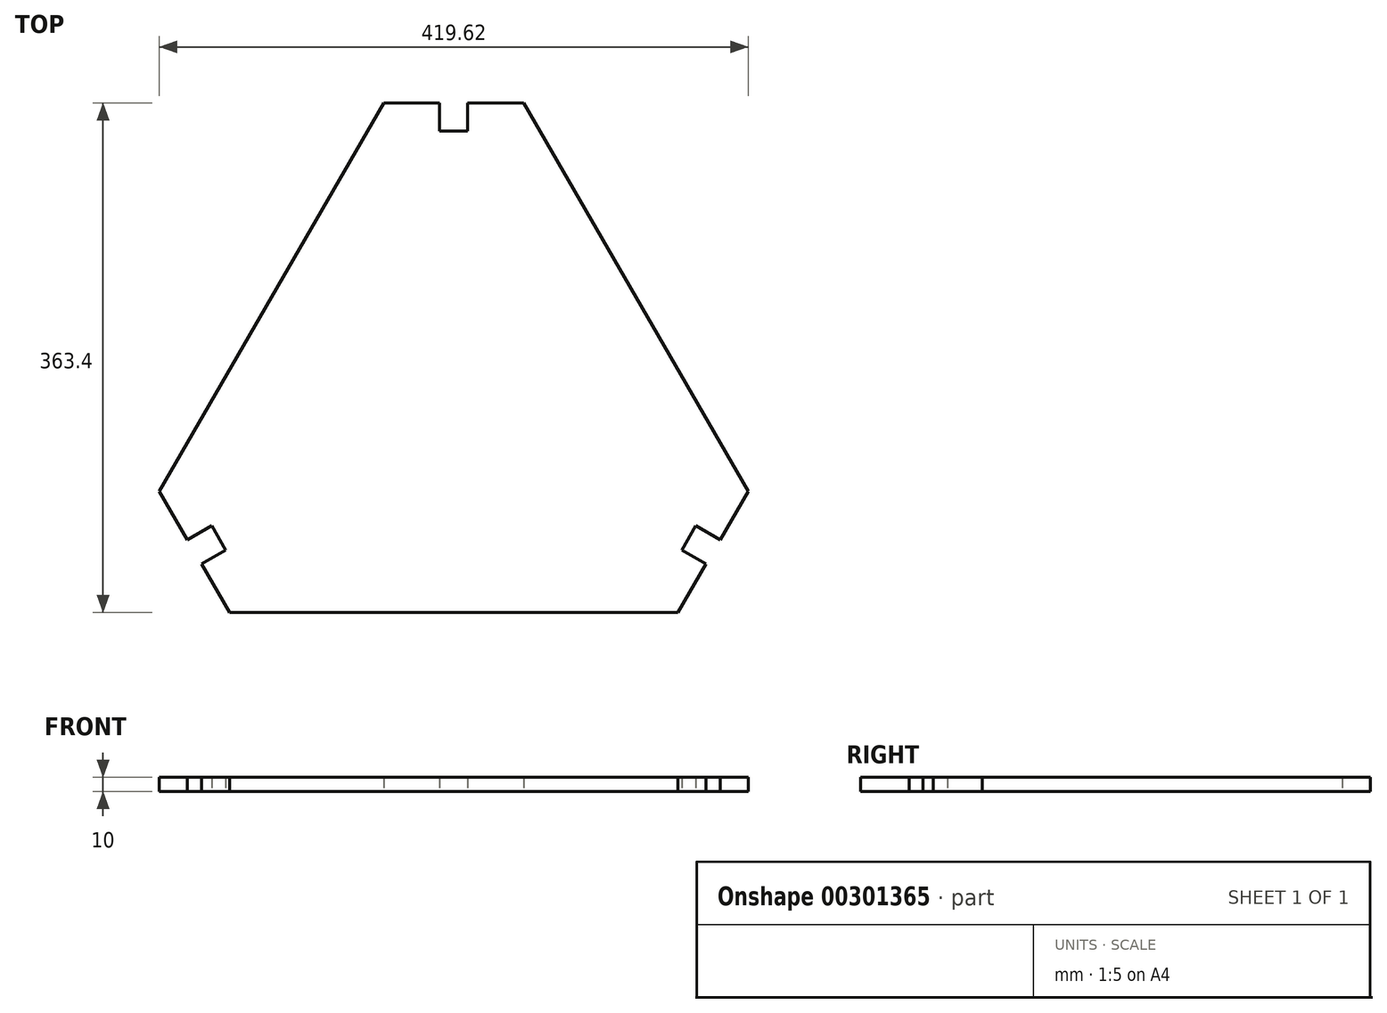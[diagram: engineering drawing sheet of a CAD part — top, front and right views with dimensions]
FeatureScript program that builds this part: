
annotation { "Feature Type Name" : "Feature", "Feature Type Description" : "" }
export const myFeature = defineFeature(function(context is Context, id is Id, definition is map)
    precondition{}
    {
        {
            var Q0;
            Q0=qCreatedBy(makeId("Top.planeOp"),FACE);
            var sketch = newSketch(context, id + "F0", { "sketchPlane" : qUnion([Q0])});
            skCircle(sketch, "E0.cCircle", {"center": v(0, 0) * mm, "radius": 213.4 * mm, "construction": true});
            skLineSegment(sketch, "E0.0", {"start": v(-50, 213.4) * mm, "end": v(50, 213.4) * mm});
            skLineSegment(sketch, "E0.1", {"start": v(50, 213.4) * mm, "end": v(209.8, -63.4) * mm});
            skLineSegment(sketch, "E0.2", {"start": v(209.8, -63.4) * mm, "end": v(159.8, -150) * mm});
            skLineSegment(sketch, "E0.3", {"start": v(159.8, -150) * mm, "end": v(-159.8, -150) * mm});
            skLineSegment(sketch, "E0.4", {"start": v(-159.8, -150) * mm, "end": v(-209.8, -63.4) * mm});
            skLineSegment(sketch, "E0.5", {"start": v(-209.8, -63.4) * mm, "end": v(-50, 213.4) * mm});
            skPoint(sketch, "E0.0.midPoint", {"position": v(0, 213.4) * mm});
            skLineSegment(sketch, "E1", {"start": v(-129.9, 75) * mm, "end": v(0, 0) * mm, "construction": true});
            skLineSegment(sketch, "E2", {"start": v(0, 213.4) * mm, "end": v(0, 0) * mm, "construction": true});
            skLineSegment(sketch, "E3.bottom", {"start": v(0, 213.4) * mm, "end": v(-10, 213.4) * mm});
            skLineSegment(sketch, "E3.top", {"start": v(0, 193.4) * mm, "end": v(-10, 193.4) * mm});
            skLineSegment(sketch, "E3.left", {"start": v(0, 213.4) * mm, "end": v(0, 193.4) * mm});
            skLineSegment(sketch, "E3.right", {"start": v(-10, 213.4) * mm, "end": v(-10, 193.4) * mm});
            skLineSegment(sketch, "E4.MirrorCS", {"start": v(0, 193.4) * mm, "end": v(10, 193.4) * mm});
            skLineSegment(sketch, "E5.MirrorCS", {"start": v(10, 213.4) * mm, "end": v(10, 193.4) * mm});
            skLineSegment(sketch, "E6.1.0", {"start": v(-189.8, -98.04) * mm, "end": v(-172.49, -88.04) * mm});
            skLineSegment(sketch, "E6.1.2", {"start": v(-184.8, -106.7) * mm, "end": v(-167.49, -96.7) * mm});
            skPoint(sketch, "E6.1.3", {"position": v(-184.8, -106.7) * mm});
            skLineSegment(sketch, "E6.1.4", {"start": v(-179.8, -115.36) * mm, "end": v(-162.49, -105.36) * mm});
            skLineSegment(sketch, "E6.1.5", {"start": v(-184.8, -106.7) * mm, "end": v(-179.8, -115.36) * mm});
            skLineSegment(sketch, "E6.1.6", {"start": v(-167.49, -96.7) * mm, "end": v(-172.49, -88.04) * mm});
            skLineSegment(sketch, "E6.1.7", {"start": v(-167.49, -96.7) * mm, "end": v(-162.49, -105.36) * mm});
            skLineSegment(sketch, "E6.1.8", {"start": v(-167.49, -96.7) * mm, "end": v(-172.49, -88.04) * mm});
            skLineSegment(sketch, "E6.2.0", {"start": v(179.8, -115.36) * mm, "end": v(162.49, -105.36) * mm});
            skLineSegment(sketch, "E6.2.2", {"start": v(184.8, -106.7) * mm, "end": v(167.49, -96.7) * mm});
            skPoint(sketch, "E6.2.3", {"position": v(184.8, -106.7) * mm});
            skLineSegment(sketch, "E6.2.4", {"start": v(189.8, -98.04) * mm, "end": v(172.49, -88.04) * mm});
            skLineSegment(sketch, "E6.2.5", {"start": v(184.8, -106.7) * mm, "end": v(189.8, -98.04) * mm});
            skLineSegment(sketch, "E6.2.6", {"start": v(167.49, -96.7) * mm, "end": v(162.49, -105.36) * mm});
            skLineSegment(sketch, "E6.2.7", {"start": v(167.49, -96.7) * mm, "end": v(172.49, -88.04) * mm});
            skLineSegment(sketch, "E6.2.8", {"start": v(167.49, -96.7) * mm, "end": v(162.49, -105.36) * mm});
            skSolve(sketch);
        }
        {
            var Q0;
            {var subQ5=sQuery(id+"F0.wireOp",EDGE,"E0.1");Q0=makeQuery(id+"F0.imprint","IMPRINT",FACE,{"disambiguationData":[TD([[makeQuery(id+"F0.imprint","IMPRINT",EDGE,{"derivedFrom":subQ5}),-1.0]])]});}
            extrude(context, id + "F1", {"entities" : qUnion([Q0]), "depth" : 10 * mm});
        }
    });
